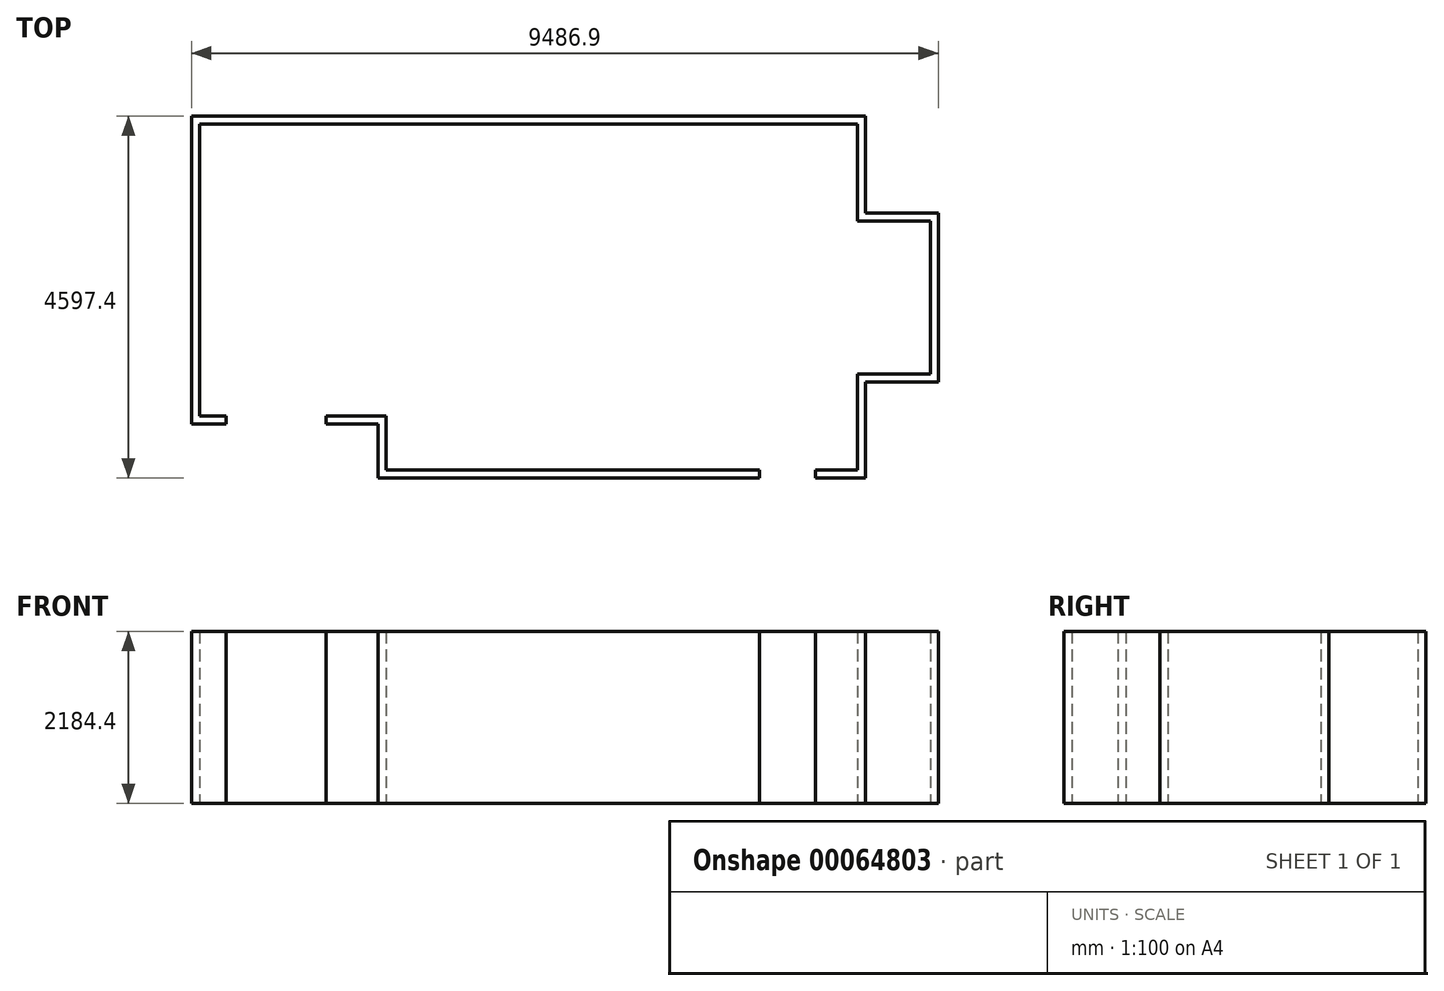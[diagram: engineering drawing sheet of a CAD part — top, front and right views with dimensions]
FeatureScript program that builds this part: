
annotation { "Feature Type Name" : "Feature", "Feature Type Description" : "" }
export const myFeature = defineFeature(function(context is Context, id is Id, definition is map)
    precondition{}
    {
        {
            var Q0;
            Q0=qCreatedBy(makeId("Top.planeOp"),FACE);
            var sketch = newSketch(context, id + "F0", { "sketchPlane" : qUnion([Q0])});
            skLineSegment(sketch, "E0", {"start": v(0, 0) * mm, "end": v(0, -3708.4) * mm});
            skLineSegment(sketch, "E1", {"start": v(0, -3708.4) * mm, "end": v(336.55, -3708.4) * mm});
            skLineSegment(sketch, "E2", {"start": v(1606.55, -3708.4) * mm, "end": v(2368.55, -3708.4) * mm});
            skLineSegment(sketch, "E3", {"start": v(2368.55, -3708.4) * mm, "end": v(2368.55, -4394.2) * mm});
            skLineSegment(sketch, "E4", {"start": v(7823.2, -4394.2) * mm, "end": v(8356.6, -4394.2) * mm});
            skLineSegment(sketch, "E5", {"start": v(8356.6, -4394.2) * mm, "end": v(8356.6, -3175) * mm});
            skLineSegment(sketch, "E6", {"start": v(8356.6, -3175) * mm, "end": v(9283.7, -3175) * mm});
            skLineSegment(sketch, "E7", {"start": v(9283.7, -3175) * mm, "end": v(9283.7, -1231.9) * mm});
            skLineSegment(sketch, "E8", {"start": v(9283.7, -1231.9) * mm, "end": v(8356.6, -1231.9) * mm});
            skLineSegment(sketch, "E9", {"start": v(8356.6, -1231.9) * mm, "end": v(8356.6, 0) * mm});
            skLineSegment(sketch, "E10", {"start": v(0, 0) * mm, "end": v(812.8, 0) * mm});
            skLineSegment(sketch, "E11", {"start": v(812.8, 0) * mm, "end": v(3048, 0) * mm});
            skLineSegment(sketch, "E12", {"start": v(3048, 0) * mm, "end": v(8356.6, 0) * mm});
            skLineSegment(sketch, "E13", {"start": v(7112, -4394.2) * mm, "end": v(2368.55, -4394.2) * mm});
            skLineSegment(sketch, "E14.0", {"start": v(7823.2, -4495.8) * mm, "end": v(8458.2, -4495.8) * mm});
            skLineSegment(sketch, "E14.2", {"start": v(7112, -4495.8) * mm, "end": v(2266.95, -4495.8) * mm});
            skLineSegment(sketch, "E14.3", {"start": v(2266.95, -3810) * mm, "end": v(2266.95, -4495.8) * mm});
            skLineSegment(sketch, "E14.4", {"start": v(1606.55, -3810) * mm, "end": v(2266.95, -3810) * mm});
            skLineSegment(sketch, "E14.5", {"start": v(8458.2, -1130.3) * mm, "end": v(8458.2, 101.6) * mm});
            skLineSegment(sketch, "E14.6", {"start": v(9385.3, -1130.3) * mm, "end": v(8458.2, -1130.3) * mm});
            skLineSegment(sketch, "E14.7", {"start": v(9385.3, -3276.6) * mm, "end": v(9385.3, -1130.3) * mm});
            skLineSegment(sketch, "E14.8", {"start": v(8458.2, -3276.6) * mm, "end": v(9385.3, -3276.6) * mm});
            skLineSegment(sketch, "E14.11", {"start": v(-101.6, 101.6) * mm, "end": v(5651.09, 101.6) * mm});
            skLineSegment(sketch, "E14.12", {"start": v(-101.6, 101.6) * mm, "end": v(-101.6, -3810) * mm});
            skLineSegment(sketch, "E14.13", {"start": v(-101.6, -3810) * mm, "end": v(336.55, -3810) * mm});
            skLineSegment(sketch, "E14.14", {"start": v(8458.2, -4495.8) * mm, "end": v(8458.2, -3276.6) * mm});
            skLineSegment(sketch, "E15", {"start": v(336.55, -3708.4) * mm, "end": v(336.55, -3810) * mm});
            skLineSegment(sketch, "E16", {"start": v(1606.55, -3810) * mm, "end": v(1606.55, -3708.4) * mm});
            skLineSegment(sketch, "E17", {"start": v(7112, -4394.2) * mm, "end": v(7112, -4495.8) * mm});
            skLineSegment(sketch, "E18", {"start": v(7823.2, -4394.2) * mm, "end": v(7823.2, -4495.8) * mm});
            skLineSegment(sketch, "E19", {"start": v(5651.09, 101.6) * mm, "end": v(8458.2, 101.6) * mm});
            skSolve(sketch);
        }
        {
            var Q0;
            Q0 = qSketchRegion(id + "F0", true);
            extrude(context, id + "F1", {"entities" : qUnion([Q0]), "depth" : 2184.4 * mm});
        }
    });
